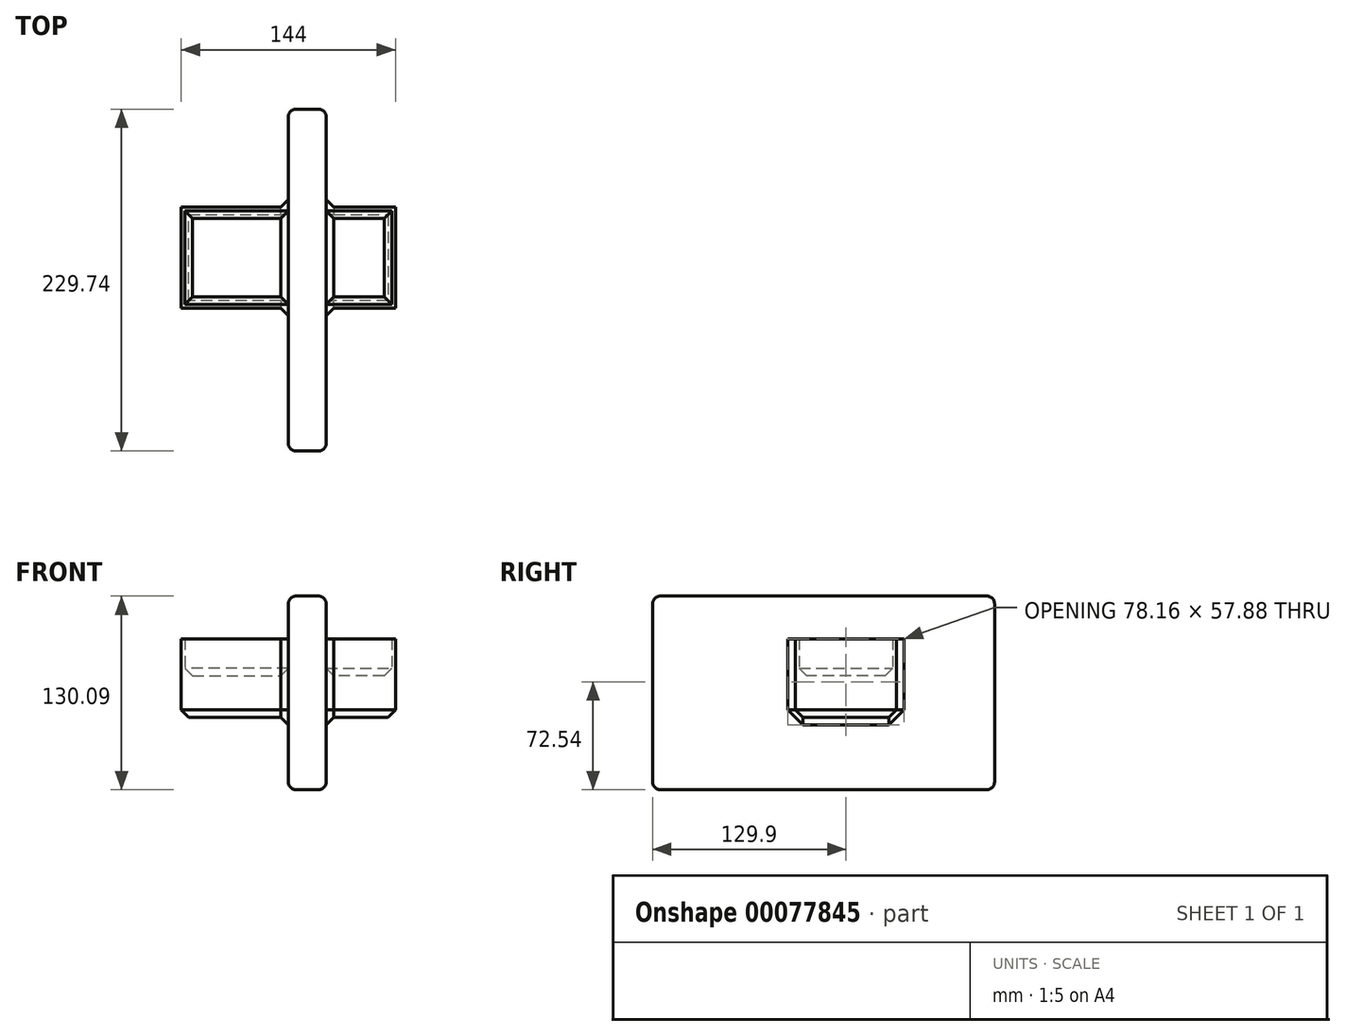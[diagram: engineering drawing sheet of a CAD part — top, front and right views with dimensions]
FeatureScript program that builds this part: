
annotation { "Feature Type Name" : "Feature", "Feature Type Description" : "" }
export const myFeature = defineFeature(function(context is Context, id is Id, definition is map)
    precondition{}
    {
        {
            var Q0;
            Q0=qCreatedBy(makeId("Top.planeOp"),FACE);
            var sketch = newSketch(context, id + "F0", { "sketchPlane" : qUnion([Q0])});
            skLineSegment(sketch, "E0.bottom", {"start": v(-72, 34) * mm, "end": v(72, 34) * mm});
            skLineSegment(sketch, "E0.top", {"start": v(-72, -34) * mm, "end": v(72, -34) * mm});
            skLineSegment(sketch, "E0.left", {"start": v(-72, 34) * mm, "end": v(-72, -34) * mm});
            skLineSegment(sketch, "E0.right", {"start": v(72, 34) * mm, "end": v(72, -34) * mm});
            skSolve(sketch);
        }
        {
            var Q0;
            Q0=makeQuery(id+"F0.imprint","IMPRINT",FACE,{"disambiguationData":[TD([[makeQuery(id+"F0.imprint","IMPRINT",EDGE,{"derivedFrom":sQuery(id+"F0.wireOp",EDGE,"E0.bottom")}),-1.0]])]});
            extrude(context, id + "F1", {"entities" : qUnion([Q0]), "depth" : 2 * mm});
        }
        {
            var Q0;
            Q0=makeQuery(id+"F1.opExtrude","CAP_FACE",FACE,{"disambiguationData":[OSD([sQuery(id+"F0.wireOp",EDGE,"E0.bottom"),sQuery(id+"F0.wireOp",EDGE,"E0.top"),sQuery(id+"F0.wireOp",EDGE,"E0.left"),sQuery(id+"F0.wireOp",EDGE,"E0.right")])],"isStart":false});
            extrude(context, id + "F2", {"entities" : qUnion([Q0]), "operationType" : NewBodyOperationType.ADD, "depth" : 25.4 * mm});
        }
        {
            var Q0;
            Q0=makeQuery(id+"F2.opExtrude","CAP_FACE",FACE,{"disambiguationData":[OSD([sQuery(id+"F0.wireOp",EDGE,"E0.bottom"),sQuery(id+"F0.wireOp",EDGE,"E0.top"),sQuery(id+"F0.wireOp",EDGE,"E0.left"),sQuery(id+"F0.wireOp",EDGE,"E0.right")])],"isStart":false});
            shell(context, id + "F3", {"entities" : qUnion([Q0]), "thickness" : 2.54 * mm});
        }
        {
            var Q0;
            Q0=makeQuery(id+"F1.opExtrude","CAP_FACE",FACE,{"disambiguationData":[OSD([sQuery(id+"F0.wireOp",EDGE,"E0.bottom"),sQuery(id+"F0.wireOp",EDGE,"E0.top"),sQuery(id+"F0.wireOp",EDGE,"E0.left"),sQuery(id+"F0.wireOp",EDGE,"E0.right")])],"isStart":true});
            extrude(context, id + "F4", {"entities" : qUnion([Q0]), "operationType" : NewBodyOperationType.ADD, "depth" : 25.4 * mm});
        }
        {
            var Q0;
            Q0=qCreatedBy(makeId("Right.planeOp"),FACE);
            var sketch = newSketch(context, id + "F5", { "sketchPlane" : qUnion([Q0])});
            skLineSegment(sketch, "E1.bottom", {"start": v(99.84, -74.08) * mm, "end": v(-129.9, -74.08) * mm});
            skLineSegment(sketch, "E1.top", {"start": v(99.84, 56) * mm, "end": v(-129.9, 56) * mm});
            skLineSegment(sketch, "E1.left", {"start": v(99.84, -74.08) * mm, "end": v(99.84, 56) * mm});
            skLineSegment(sketch, "E1.right", {"start": v(-129.9, -74.08) * mm, "end": v(-129.9, 56) * mm});
            skSolve(sketch);
        }
        {
            var Q0;
            Q0=makeQuery(id+"F5.imprint","IMPRINT",FACE,{"disambiguationData":[TD([[makeQuery(id+"F5.imprint","IMPRINT",EDGE,{"derivedFrom":sQuery(id+"F5.wireOp",EDGE,"E1.bottom")}),-1.0]])]});
            extrude(context, id + "F6", {"entities" : qUnion([Q0]), "operationType" : NewBodyOperationType.ADD, "depth" : 25.4 * mm});
        }
        {
            var Q0;
            Q0=makeQuery(id+"F6.opExtrude","SWEPT_FACE",FACE,{"disambiguationData":[OSD([sQuery(id+"F5.wireOp",EDGE,"E1.bottom")])]});
            fillet(context, id + "F7", {"entities" : qUnion([Q0]), "radius" : 5.08 * mm, "tangentPropagation" : true, "allowEdgeOverflow" : false});
        }
        {
            var Q0;
            Q0=makeQuery(id+"F6.opExtrude","SWEPT_FACE",FACE,{"disambiguationData":[OSD([sQuery(id+"F5.wireOp",EDGE,"E1.top")])]});
            fillet(context, id + "F8", {"entities" : qUnion([Q0]), "radius" : 5.08 * mm, "tangentPropagation" : true, "allowEdgeOverflow" : false});
        }
        {
            var Q0;
            {var subQ0=sQuery(id+"F0.wireOp",EDGE,"E0.bottom");var subQ1=sQuery(id+"F0.wireOp",EDGE,"E0.left");var subQ2=sQuery(id+"F0.wireOp",EDGE,"E0.top");Q0=makeQuery(id+"F6.boolean.opBoolean","SPLIT",FACE,{"disambiguationData":[TD([makeQuery(id+"F1.opExtrude","SWEPT_FACE",FACE,{"disambiguationData":[OSD([subQ1])]})])],"derivedFrom":makeQuery(id+"F4.opExtrude","CAP_FACE",FACE,{"disambiguationData":[OSD([subQ0,subQ2,subQ1,sQuery(id+"F0.wireOp",EDGE,"E0.right")])],"isStart":false})});}
            chamfer(context, id + "F9", {"entities" : qUnion([Q0]), "width" : 5.08 * mm, "tangentPropagation" : true});
        }
        {
            var Q0;
            {var subQ0=sQuery(id+"F0.wireOp",EDGE,"E0.bottom");var subQ1=sQuery(id+"F0.wireOp",EDGE,"E0.right");var subQ2=sQuery(id+"F0.wireOp",EDGE,"E0.top");Q0=makeQuery(id+"F6.boolean.opBoolean","SPLIT",FACE,{"disambiguationData":[TD([makeQuery(id+"F1.opExtrude","SWEPT_FACE",FACE,{"disambiguationData":[OSD([subQ1])]})])],"derivedFrom":makeQuery(id+"F4.opExtrude","CAP_FACE",FACE,{"disambiguationData":[OSD([subQ0,subQ2,sQuery(id+"F0.wireOp",EDGE,"E0.left"),subQ1])],"isStart":false})});}
            chamfer(context, id + "F10", {"entities" : qUnion([Q0]), "width" : 5.08 * mm, "tangentPropagation" : true});
        }
        {
            var Q0;
            {var subQ0=sQuery(id+"F0.wireOp",EDGE,"E0.bottom");var subQ1=sQuery(id+"F0.wireOp",EDGE,"E0.top");var subQ2=sQuery(id+"F0.wireOp",EDGE,"E0.left");Q0=makeQuery(id+"F6.boolean.opBoolean","SPLIT",FACE,{"disambiguationData":[TD([makeQuery(id+"F3.opShell","OFFSET_FACE",FACE,{"disambiguationData":[OSD([subQ2])]})])],"derivedFrom":makeQuery(id+"F3.opShell","OFFSET_FACE",FACE,{"disambiguationData":[OSD([subQ0,subQ1,subQ2,sQuery(id+"F0.wireOp",EDGE,"E0.right")])]})});}
            chamfer(context, id + "F11", {"entities" : qUnion([Q0]), "width" : 5.08 * mm, "tangentPropagation" : true});
        }
        {
            var Q0;
            {var subQ0=sQuery(id+"F0.wireOp",EDGE,"E0.bottom");var subQ1=sQuery(id+"F0.wireOp",EDGE,"E0.top");var subQ2=sQuery(id+"F0.wireOp",EDGE,"E0.right");Q0=makeQuery(id+"F6.boolean.opBoolean","SPLIT",FACE,{"disambiguationData":[TD([makeQuery(id+"F3.opShell","OFFSET_FACE",FACE,{"disambiguationData":[OSD([subQ2])]})])],"derivedFrom":makeQuery(id+"F3.opShell","OFFSET_FACE",FACE,{"disambiguationData":[OSD([subQ0,subQ1,sQuery(id+"F0.wireOp",EDGE,"E0.left"),subQ2])]})});}
            chamfer(context, id + "F12", {"entities" : qUnion([Q0]), "width" : 5.08 * mm, "tangentPropagation" : true});
        }
        {
            var Q0;
            Q0=makeQuery(id+"F6.opExtrude","SWEPT_FACE",FACE,{"disambiguationData":[OSD([sQuery(id+"F5.wireOp",EDGE,"E1.left")])]});
            fillet(context, id + "F13", {"entities" : qUnion([Q0]), "radius" : 5.08 * mm, "tangentPropagation" : true, "allowEdgeOverflow" : false});
        }
        {
            var Q0;
            Q0=makeQuery(id+"F6.opExtrude","SWEPT_FACE",FACE,{"disambiguationData":[OSD([sQuery(id+"F5.wireOp",EDGE,"E1.right")])]});
            fillet(context, id + "F14", {"entities" : qUnion([Q0]), "radius" : 5.08 * mm, "tangentPropagation" : true, "allowEdgeOverflow" : false});
        }
    });
